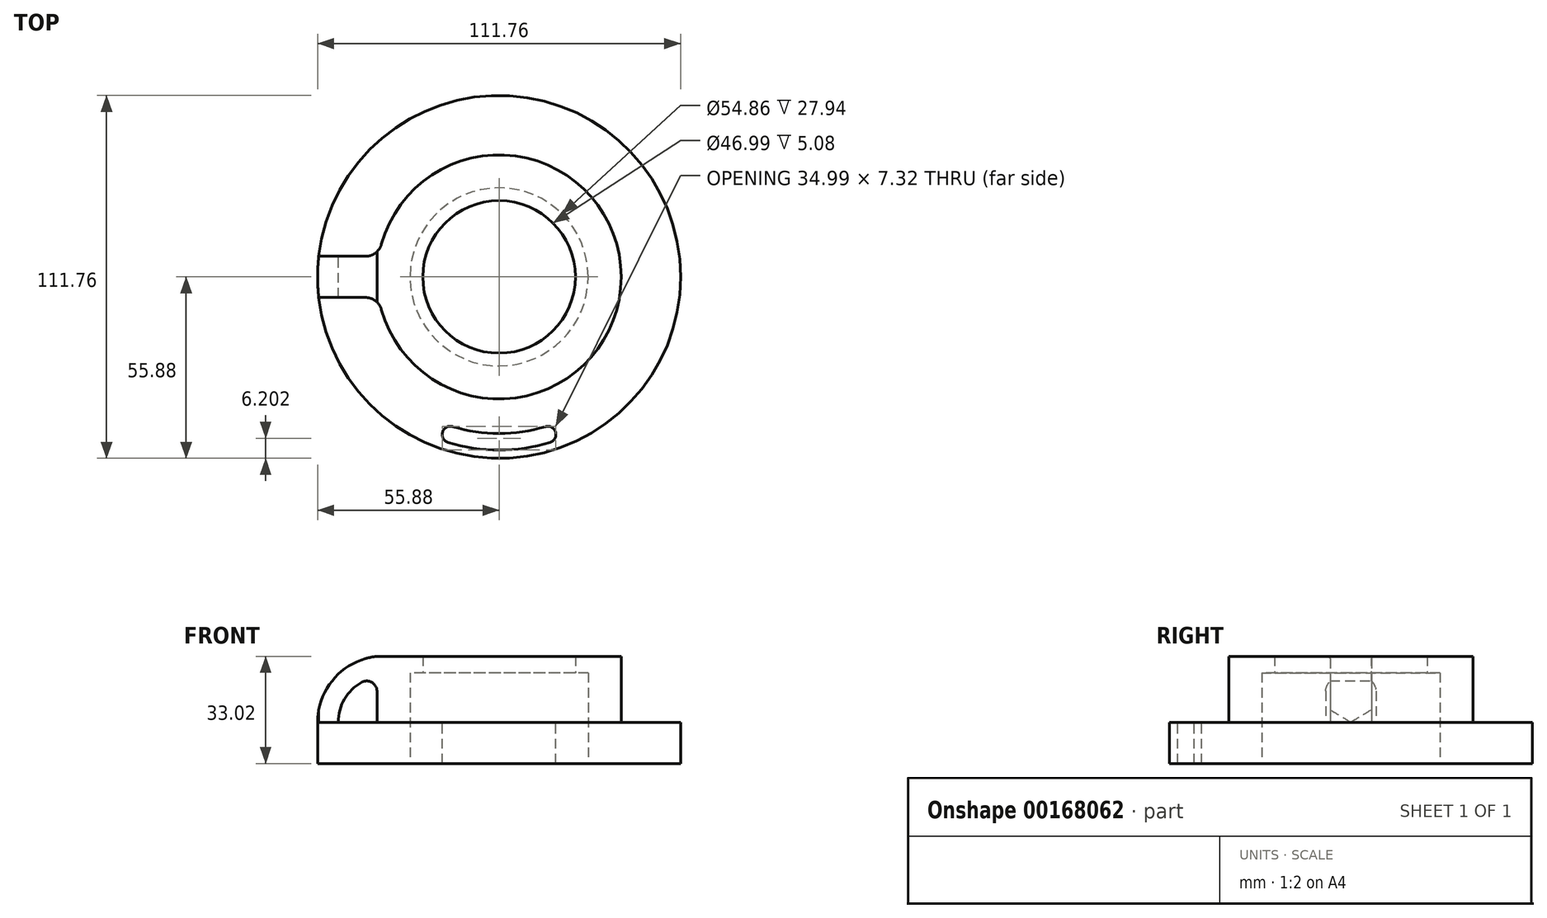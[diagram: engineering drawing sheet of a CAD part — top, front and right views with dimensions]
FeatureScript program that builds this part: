
annotation { "Feature Type Name" : "Feature", "Feature Type Description" : "" }
export const myFeature = defineFeature(function(context is Context, id is Id, definition is map)
    precondition{}
    {
        {
            var Q0;
            Q0=qCreatedBy(makeId("Top.planeOp"),FACE);
            var sketch = newSketch(context, id + "F0", { "sketchPlane" : qUnion([Q0])});
            skCircle(sketch, "E0", {"center": v(0, 0) * mm, "radius": 55.88 * mm});
            skCircle(sketch, "E1", {"center": v(0, 0) * mm, "radius": 27.43 * mm});
            skSolve(sketch);
        }
        {
            var Q0;
            Q0=qSketchRegion(id+"F0",true);
            extrude(context, id + "F1", {"entities" : qUnion([Q0]), "depth" : 12.7 * mm});
        }
        {
            var Q0;
            Q0=makeQuery(id+"F1.opExtrude","CAP_FACE",FACE,{"disambiguationData":[OSD([sQuery(id+"F0.wireOp",EDGE,"E0"),sQuery(id+"F0.wireOp",EDGE,"E1")])],"isStart":false});
            var sketch = newSketch(context, id + "F2", { "sketchPlane" : qUnion([Q0])});
            skCircle(sketch, "E2", {"center": v(0, 0) * mm, "radius": 37.6 * mm});
            skCircle(sketch, "E3", {"center": v(0, 0) * mm, "radius": 27.43 * mm});
            skSolve(sketch);
        }
        {
            var Q0;
            Q0=qSketchRegion(id+"F2",true);
            extrude(context, id + "F3", {"entities" : qUnion([Q0]), "operationType" : NewBodyOperationType.ADD, "depth" : 15.24 * mm});
        }
        {
            var Q0;
            Q0=makeQuery(id+"F3.opExtrude","CAP_FACE",FACE,{"disambiguationData":[OSD([sQuery(id+"F2.wireOp",EDGE,"E2"),sQuery(id+"F2.wireOp",EDGE,"E3")])],"isStart":false});
            var sketch = newSketch(context, id + "F4", { "sketchPlane" : qUnion([Q0])});
            skCircle(sketch, "E4.0", {"center": v(0, 0) * mm, "radius": 37.6 * mm});
            skCircle(sketch, "E5", {"center": v(0, 0) * mm, "radius": 23.5 * mm});
            skSolve(sketch);
        }
        {
            var Q0;
            Q0=qSketchRegion(id+"F4",true);
            extrude(context, id + "F5", {"entities" : qUnion([Q0]), "operationType" : NewBodyOperationType.ADD, "depth" : 5.08 * mm});
        }
        {
            var Q0;
            Q0=makeQuery(id+"F1.opExtrude","CAP_FACE",FACE,{"disambiguationData":[OSD([sQuery(id+"F0.wireOp",EDGE,"E0"),sQuery(id+"F0.wireOp",EDGE,"E1")])],"isStart":false});
            var sketch = newSketch(context, id + "F6", { "sketchPlane" : qUnion([Q0])});
            skArc(sketch, "E6", {"start": v(17.37, -47.74) * mm, "mid": v(0, -50.8) * mm, "end": v(-17.37, -47.74) * mm, "construction": true});
            skLineSegment(sketch, "E7", {"start": v(-17.37, -47.74) * mm, "end": v(0, 0) * mm, "construction": true});
            skLineSegment(sketch, "E8", {"start": v(17.37, -47.74) * mm, "end": v(0, 0) * mm, "construction": true});
            skArc(sketch, "E9", {"start": v(-16.5, -45.35) * mm, "mid": v(0, -48.26) * mm, "end": v(16.5, -45.35) * mm});
            skArc(sketch, "E10", {"start": v(-18.24, -50.12) * mm, "mid": v(0, -53.34) * mm, "end": v(18.24, -50.12) * mm});
            skLineSegment(sketch, "E11", {"start": v(-18.24, -50.12) * mm, "end": v(-17.37, -47.74) * mm, "construction": true});
            skLineSegment(sketch, "E12", {"start": v(18.24, -50.12) * mm, "end": v(17.37, -47.74) * mm, "construction": true});
            skLineSegment(sketch, "E13", {"start": v(16.5, -45.35) * mm, "end": v(18.24, -50.12) * mm});
            skLineSegment(sketch, "E14", {"start": v(-18.24, -50.12) * mm, "end": v(-16.5, -45.35) * mm});
            skSolve(sketch);
        }
        {
            var Q0;
            Q0=qSketchRegion(id+"F6",true);
            extrude(context, id + "F7", {"entities" : qUnion([Q0]), "operationType" : NewBodyOperationType.REMOVE, "endBound" : BoundingType.THROUGH_ALL, "oppositeDirection" : true, "depth" : 25.4 * mm});
        }
        {
            var Q0;
            Q0=makeQuery(id+"F7.boolean.opBoolean","COPY",EDGE,{"derivedFrom":makeQuery(id+"F7.opExtrude","SWEPT_EDGE",EDGE,{"disambiguationData":[OSD([sQuery(id+"F6.wireOp",EDGE,"E10"),sQuery(id+"F6.wireOp",EDGE,"E14")])]})});
            var Q1;
            Q1=makeQuery(id+"F7.boolean.opBoolean","COPY",EDGE,{"derivedFrom":makeQuery(id+"F7.opExtrude","SWEPT_EDGE",EDGE,{"disambiguationData":[OSD([sQuery(id+"F6.wireOp",EDGE,"E9"),sQuery(id+"F6.wireOp",EDGE,"E14")])]})});
            var Q2;
            Q2=makeQuery(id+"F7.boolean.opBoolean","COPY",EDGE,{"derivedFrom":makeQuery(id+"F7.opExtrude","SWEPT_EDGE",EDGE,{"disambiguationData":[OSD([sQuery(id+"F6.wireOp",EDGE,"E10"),sQuery(id+"F6.wireOp",EDGE,"E13")])]})});
            var Q3;
            Q3=makeQuery(id+"F7.boolean.opBoolean","COPY",EDGE,{"derivedFrom":makeQuery(id+"F7.opExtrude","SWEPT_EDGE",EDGE,{"disambiguationData":[OSD([sQuery(id+"F6.wireOp",EDGE,"E9"),sQuery(id+"F6.wireOp",EDGE,"E13")])]})});
            fillet(context, id + "F8", {"entities" : qUnion([Q0, Q1, Q2, Q3]), "radius" : 2.54 * mm, "tangentPropagation" : true, "allowEdgeOverflow" : false});
        }
        {
            var Q0;
            Q0=qCreatedBy(makeId("Front.planeOp"),FACE);
            var sketch = newSketch(context, id + "F9", { "sketchPlane" : qUnion([Q0])});
            skLineSegment(sketch, "E15.0", {"start": v(-55.88, 12.7) * mm, "end": v(55.88, 12.7) * mm, "construction": true});
            skLineSegment(sketch, "E16.0", {"start": v(-37.6, 33.02) * mm, "end": v(37.6, 33.02) * mm, "construction": true});
            skLineSegment(sketch, "E17", {"start": v(-49.53, 12.7) * mm, "end": v(-55.88, 12.7) * mm, "construction": true});
            skArc(sketch, "E18", {"start": v(-37.6, 33.02) * mm, "mid": v(-50.63, 26.37) * mm, "end": v(-55.88, 12.7) * mm});
            skLineSegment(sketch, "E19", {"start": v(-37.6, 33.02) * mm, "end": v(-37.6, 26.67) * mm, "construction": true});
            skArc(sketch, "E20", {"start": v(-37.6, 26.67) * mm, "mid": v(-46.14, 21.89) * mm, "end": v(-49.53, 12.7) * mm});
            skLineSegment(sketch, "E21", {"start": v(-55.88, 12.7) * mm, "end": v(-55.88, 10.16) * mm});
            skLineSegment(sketch, "E22", {"start": v(-55.88, 10.16) * mm, "end": v(-49.53, 10.16) * mm});
            skLineSegment(sketch, "E23", {"start": v(-49.53, 10.16) * mm, "end": v(-49.53, 12.7) * mm, "construction": true});
            skLineSegment(sketch, "E24", {"start": v(-37.6, 33.02) * mm, "end": v(-35.05, 33.02) * mm});
            skLineSegment(sketch, "E25", {"start": v(-35.05, 33.02) * mm, "end": v(-35.05, 26.67) * mm});
            skLineSegment(sketch, "E26", {"start": v(-35.05, 26.67) * mm, "end": v(-37.6, 26.67) * mm});
            skLineSegment(sketch, "E27", {"start": v(-37.6, 26.67) * mm, "end": v(-35.05, 26.67) * mm});
            skLineSegment(sketch, "E28", {"start": v(-49.53, 12.7) * mm, "end": v(-37.6, 12.7) * mm});
            skLineSegment(sketch, "E29", {"start": v(-37.6, 12.7) * mm, "end": v(-37.6, 26.67) * mm});
            skLineSegment(sketch, "E30", {"start": v(-49.53, 10.16) * mm, "end": v(-33.8, 10.16) * mm});
            skLineSegment(sketch, "E31", {"start": v(-33.8, 10.16) * mm, "end": v(-35.05, 26.67) * mm});
            skSolve(sketch);
        }
        {
            var Q0;
            Q0=qSketchRegion(id+"F9",true);
            extrude(context, id + "F10", {"entities" : qUnion([Q0]), "operationType" : NewBodyOperationType.ADD, "depth" : 6.35 * mm, "hasSecondDirection" : true, "secondDirectionOppositeDirection" : true, "secondDirectionDepth" : 6.35 * mm});
        }
        {
            var Q0;
            Q0=makeQuery(id+"F10.opExtrude","SWEPT_EDGE",EDGE,{"disambiguationData":[OSD([sQuery(id+"F9.wireOp",EDGE,"E20"),sQuery(id+"F9.wireOp",EDGE,"E23")])]});
            var Q1;
            Q1=makeQuery(id+"F10.opExtrude","SWEPT_EDGE",EDGE,{"disambiguationData":[OSD([sQuery(id+"F9.wireOp",EDGE,"E28"),sQuery(id+"F9.wireOp",EDGE,"E29")])]});
            fillet(context, id + "F11", {"entities" : qUnion([Q0, Q1]), "radius" : 3.17 * mm, "tangentPropagation" : true, "allowEdgeOverflow" : false});
        }
        {
            var Q0;
            Q0=makeQuery(id+"F10.boolean.opBoolean","INTERSECT",EDGE,{"derivedFrom":[makeQuery(id+"F5.boolean.opBoolean","MERGE",FACE,{"derivedFrom":[makeQuery(id+"F3.opExtrude","SWEPT_FACE",FACE,{"disambiguationData":[OSD([sQuery(id+"F2.wireOp",EDGE,"E2")])]}),makeQuery(id+"F5.opExtrude","SWEPT_FACE",FACE,{"disambiguationData":[OSD([sQuery(id+"F4.wireOp",EDGE,"E4.0")])]})]}),makeQuery(id+"F10.opExtrude","CAP_FACE",FACE,{"disambiguationData":[OSD([sQuery(id+"F9.wireOp",EDGE,"E18"),sQuery(id+"F9.wireOp",EDGE,"E20"),sQuery(id+"F9.wireOp",EDGE,"E21"),sQuery(id+"F9.wireOp",EDGE,"E22"),sQuery(id+"F9.wireOp",EDGE,"E23"),sQuery(id+"F9.wireOp",EDGE,"E24"),sQuery(id+"F9.wireOp",EDGE,"E25"),sQuery(id+"F9.wireOp",EDGE,"E27")])],"isStart":false})]});
            var Q1;
            Q1=makeQuery(id+"F10.boolean.opBoolean","INTERSECT",EDGE,{"derivedFrom":[makeQuery(id+"F5.boolean.opBoolean","MERGE",FACE,{"derivedFrom":[makeQuery(id+"F3.opExtrude","SWEPT_FACE",FACE,{"disambiguationData":[OSD([sQuery(id+"F2.wireOp",EDGE,"E2")])]}),makeQuery(id+"F5.opExtrude","SWEPT_FACE",FACE,{"disambiguationData":[OSD([sQuery(id+"F4.wireOp",EDGE,"E4.0")])]})]}),makeQuery(id+"F10.opExtrude","CAP_FACE",FACE,{"disambiguationData":[OSD([sQuery(id+"F9.wireOp",EDGE,"E18"),sQuery(id+"F9.wireOp",EDGE,"E20"),sQuery(id+"F9.wireOp",EDGE,"E21"),sQuery(id+"F9.wireOp",EDGE,"E22"),sQuery(id+"F9.wireOp",EDGE,"E23"),sQuery(id+"F9.wireOp",EDGE,"E24"),sQuery(id+"F9.wireOp",EDGE,"E25"),sQuery(id+"F9.wireOp",EDGE,"E27")])],"isStart":true})]});
            fillet(context, id + "F12", {"entities" : qUnion([Q0, Q1]), "radius" : 5.08 * mm, "tangentPropagation" : true, "allowEdgeOverflow" : false});
        }
        {
            var Q0;
            Q0=makeQuery(id+"F1.opExtrude","CAP_FACE",FACE,{"disambiguationData":[OSD([sQuery(id+"F0.wireOp",EDGE,"E0"),sQuery(id+"F0.wireOp",EDGE,"E1")])],"isStart":true});
            var sketch = newSketch(context, id + "F13", { "sketchPlane" : qUnion([Q0])});
            skCircle(sketch, "E32.0", {"center": v(0, 0) * mm, "radius": 55.88 * mm});
            skCircle(sketch, "E33.0", {"center": v(0, 0) * mm, "radius": 62.23 * mm});
            skSolve(sketch);
        }
        {
            var Q0;
            Q0=qSketchRegion(id+"F13",true);
            extrude(context, id + "F14", {"entities" : qUnion([Q0]), "operationType" : NewBodyOperationType.REMOVE, "endBound" : BoundingType.THROUGH_ALL, "oppositeDirection" : true, "depth" : 25.4 * mm});
        }
    });
